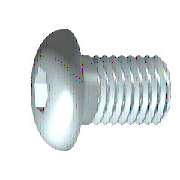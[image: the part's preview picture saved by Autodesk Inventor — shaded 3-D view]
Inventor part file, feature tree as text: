
AUTODESK INVENTOR PART (.ipt)
format: ipt  version: 2024.2 (Build 282272000, 272)  size: 207,872 bytes
history: native  units: mm (DEFAULTED — no unit token found)
features: extrude x1, plane x1, fillet x1
ambient origin geometry x7: Origin, YZ Plane, XY Plane, X Axis, Y Axis, Z Axis, Center Point
bodies: Solid1 (feature_tree), Body (feature_tree)
feature tree (3):
  extrude  "Slot"  Depth=6.5mm
  plane  "Work Plane1"
  fillet  "Fillet2"  Radius=0.306825mm
